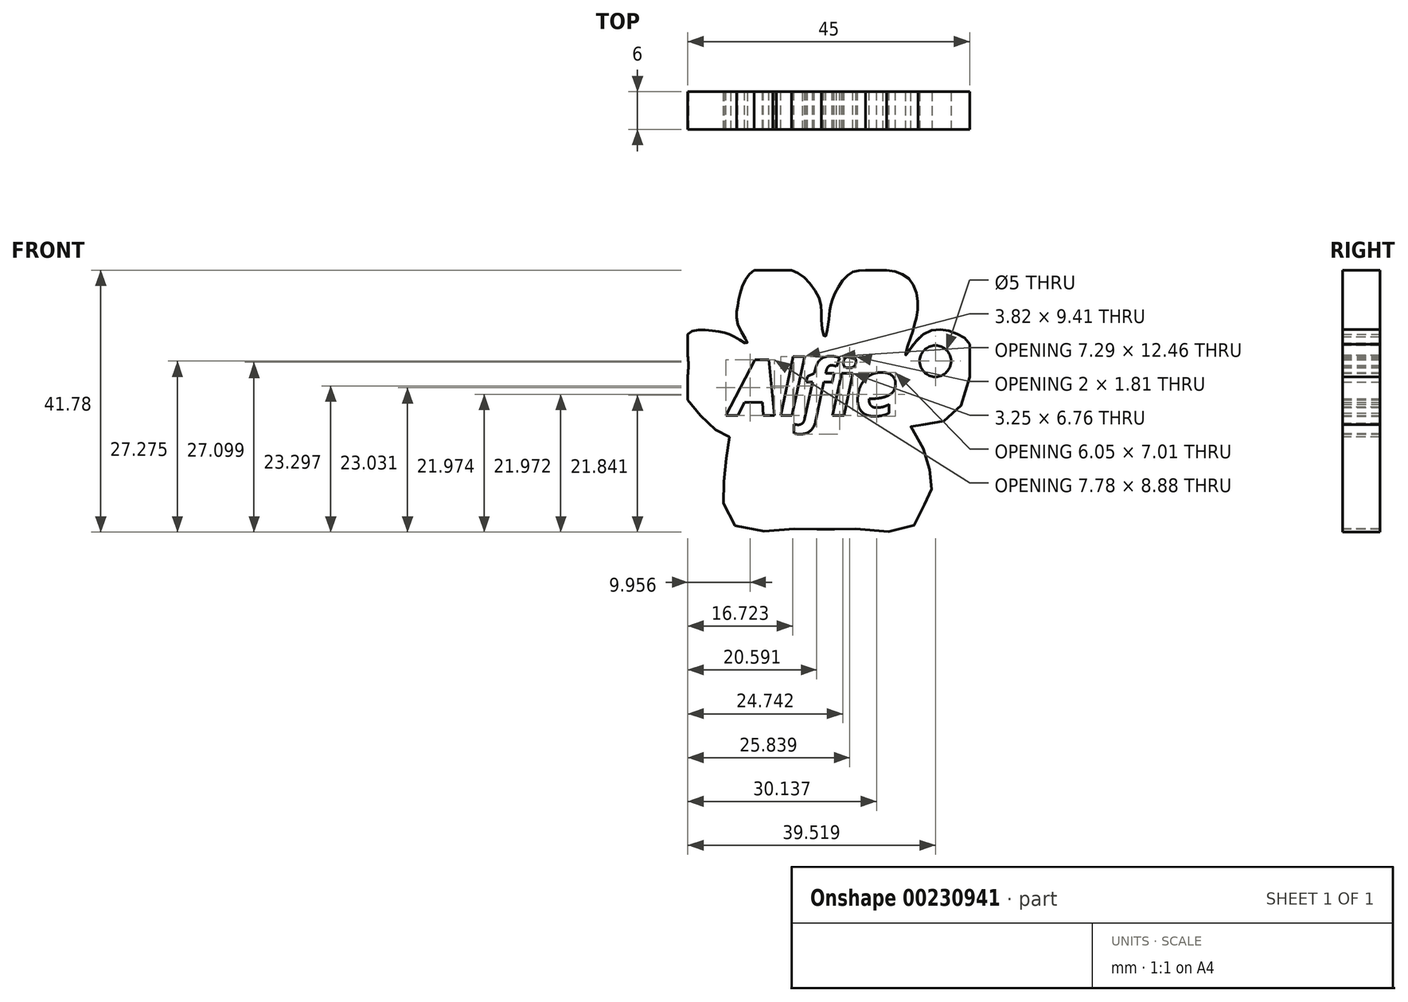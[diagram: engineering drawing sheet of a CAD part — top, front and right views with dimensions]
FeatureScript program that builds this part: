
annotation { "Feature Type Name" : "Feature", "Feature Type Description" : "" }
export const myFeature = defineFeature(function(context is Context, id is Id, definition is map)
    precondition{}
    {
        {
            var Q0;
            Q0=qCreatedBy(makeId("Front.planeOp"),FACE);
            var sketch = newSketch(context, id + "F0", { "sketchPlane" : qUnion([Q0])});
            skLineSegment(sketch, "E0.bottom", {"start": v(-5.8, 13.59) * mm, "end": v(39.2, 13.59) * mm});
            skLineSegment(sketch, "E0.top", {"start": v(-5.8, -31.41) * mm, "end": v(39.2, -31.41) * mm});
            skLineSegment(sketch, "E0.left", {"start": v(-5.8, 13.59) * mm, "end": v(-5.8, -31.41) * mm});
            skLineSegment(sketch, "E0.right", {"start": v(39.2, 13.59) * mm, "end": v(39.2, -31.41) * mm});
            skPoint(sketch, "E1.34.internal.snap0", {"position": v(39.2, -8.91) * mm});
            skFitSpline(sketch, "E1", {"points": [v(-4.05, -9.34) * mm, v(-5.8, -7.09) * mm, v(-5.8, -3.27) * mm, v(-5.8, 0) * mm, v(-5.8, 3.35) * mm, v(-3.2, 4.06) * mm, v(0, 3.63) * mm, v(2, 2.79) * mm, v(3.7, 1.94) * mm, v(2.29, 4.76) * mm, v(2.15, 7.72) * mm, v(2.85, 10.82) * mm, v(4.83, 13.59) * mm, v(7.79, 13.59) * mm, v(10.75, 13.59) * mm, v(13.43, 11.8) * mm, v(15.4, 8.43) * mm, v(15.54, 5.18) * mm, v(16.1, 2.93) * mm, v(16.8, 6.6) * mm, v(17.23, 8.7) * mm, v(18.36, 11.1) * mm, v(20.33, 13.22) * mm, v(22.59, 13.59) * mm, v(25.97, 13.59) * mm, v(29.36, 12.37) * mm, v(30.9, 8.85) * mm, v(30.48, 5.18) * mm, v(29.64, 2.36) * mm, v(28.93, 0) * mm, v(31.61, 3.21) * mm, v(35.84, 3.92) * mm, v(39.2, 1.8) * mm, v(39.2, -3.42) * mm, v(37.25, -8.91) * mm, v(34.3, -10.75) * mm, v(31.33, -11.03) * mm, v(29.78, -11.03) * mm, v(31.33, -13.99) * mm, v(32.6, -17.37) * mm, v(33.16, -20.47) * mm, v(32.88, -22.3) * mm, v(31.61, -24.56) * mm, v(29.64, -27.76) * mm, v(22.87, -27.76) * mm, v(18.22, -27.76) * mm, v(16.7, -27.76) * mm, v(13.85, -27.76) * mm, v(9.76, -27.76) * mm, v(2.85, -27.76) * mm, v(0, -24.28) * mm, v(0, -20.61) * mm, v(0, -17.8) * mm, v(1.02, -13.14) * mm, v(0, -13) * mm, v(-1.8, -11.3) * mm, v(-4.05, -9.34) * mm]});
            skText(sketch, "E2", { "text": "Alfie", "fontName": "OpenSans-BoldItalic.ttf"});
            const initialGuessF0  = {"E2": [0.00102, -0.0096, 1, 0, 0.00892]};
            skSetInitialGuess(sketch, initialGuessF0);
            skSolve(sketch);
        }
        {
            var Q0;
            Q0=makeQuery(id+"F0.imprint","IMPRINT",FACE,{"disambiguationData":[TD([[makeQuery(id+"F0.imprint","IMPRINT",EDGE,{"derivedFrom":sQuery(id+"F0.wireOp",EDGE,"E2.sketch_text.stroke-0")}),1.0]])]});
            var Q1;
            Q1=sQuery(id+"F0.wireOp",EDGE,"E1");
            extrude(context, id + "F1", {"entities" : qUnion([Q0]), "surfaceEntities" : qUnion([Q1]), "depth" : 6 * mm});
        }
        {
            var Q0;
            Q0=makeQuery(id+"F1.opExtrude","CAP_FACE",FACE,{"disambiguationData":[OSD([sQuery(id+"F0.wireOp",EDGE,"E0.bottom"),sQuery(id+"F0.wireOp",EDGE,"E0.left"),sQuery(id+"F0.wireOp",EDGE,"E0.right"),sQuery(id+"F0.wireOp",EDGE,"E1"),sQuery(id+"F0.wireOp",EDGE,"E2.sketch_text.stroke-0"),sQuery(id+"F0.wireOp",EDGE,"E2.sketch_text.stroke-1"),sQuery(id+"F0.wireOp",EDGE,"E2.sketch_text.stroke-2"),sQuery(id+"F0.wireOp",EDGE,"E2.sketch_text.stroke-3"),sQuery(id+"F0.wireOp",EDGE,"E2.sketch_text.stroke-4"),sQuery(id+"F0.wireOp",EDGE,"E2.sketch_text.stroke-5"),sQuery(id+"F0.wireOp",EDGE,"E2.sketch_text.stroke-6"),sQuery(id+"F0.wireOp",EDGE,"E2.sketch_text.stroke-7"),sQuery(id+"F0.wireOp",EDGE,"E2.sketch_text.stroke-14"),sQuery(id+"F0.wireOp",EDGE,"E2.sketch_text.stroke-15"),sQuery(id+"F0.wireOp",EDGE,"E2.sketch_text.stroke-16"),sQuery(id+"F0.wireOp",EDGE,"E2.sketch_text.stroke-17"),sQuery(id+"F0.wireOp",EDGE,"E2.sketch_text.stroke-18"),sQuery(id+"F0.wireOp",EDGE,"E2.sketch_text.stroke-19"),sQuery(id+"F0.wireOp",EDGE,"E2.sketch_text.stroke-20"),sQuery(id+"F0.wireOp",EDGE,"E2.sketch_text.stroke-21"),sQuery(id+"F0.wireOp",EDGE,"E2.sketch_text.stroke-22"),sQuery(id+"F0.wireOp",EDGE,"E2.sketch_text.stroke-23"),sQuery(id+"F0.wireOp",EDGE,"E2.sketch_text.stroke-24"),sQuery(id+"F0.wireOp",EDGE,"E2.sketch_text.stroke-25"),sQuery(id+"F0.wireOp",EDGE,"E2.sketch_text.stroke-26"),sQuery(id+"F0.wireOp",EDGE,"E2.sketch_text.stroke-27"),sQuery(id+"F0.wireOp",EDGE,"E2.sketch_text.stroke-28"),sQuery(id+"F0.wireOp",EDGE,"E2.sketch_text.stroke-29"),sQuery(id+"F0.wireOp",EDGE,"E2.sketch_text.stroke-30"),sQuery(id+"F0.wireOp",EDGE,"E2.sketch_text.stroke-31"),sQuery(id+"F0.wireOp",EDGE,"E2.sketch_text.stroke-32"),sQuery(id+"F0.wireOp",EDGE,"E2.sketch_text.stroke-33"),sQuery(id+"F0.wireOp",EDGE,"E2.sketch_text.stroke-34"),sQuery(id+"F0.wireOp",EDGE,"E2.sketch_text.stroke-35"),sQuery(id+"F0.wireOp",EDGE,"E2.sketch_text.stroke-36"),sQuery(id+"F0.wireOp",EDGE,"E2.sketch_text.stroke-37"),sQuery(id+"F0.wireOp",EDGE,"E2.sketch_text.stroke-38"),sQuery(id+"F0.wireOp",EDGE,"E2.sketch_text.stroke-39"),sQuery(id+"F0.wireOp",EDGE,"E2.sketch_text.stroke-40"),sQuery(id+"F0.wireOp",EDGE,"E2.sketch_text.stroke-41"),sQuery(id+"F0.wireOp",EDGE,"E2.sketch_text.stroke-42"),sQuery(id+"F0.wireOp",EDGE,"E2.sketch_text.stroke-43"),sQuery(id+"F0.wireOp",EDGE,"E2.sketch_text.stroke-44"),sQuery(id+"F0.wireOp",EDGE,"E2.sketch_text.stroke-45"),sQuery(id+"F0.wireOp",EDGE,"E2.sketch_text.stroke-46"),sQuery(id+"F0.wireOp",EDGE,"E2.sketch_text.stroke-47"),sQuery(id+"F0.wireOp",EDGE,"E2.sketch_text.stroke-48"),sQuery(id+"F0.wireOp",EDGE,"E2.sketch_text.stroke-49"),sQuery(id+"F0.wireOp",EDGE,"E2.sketch_text.stroke-50"),sQuery(id+"F0.wireOp",EDGE,"E2.sketch_text.stroke-51"),sQuery(id+"F0.wireOp",EDGE,"E2.sketch_text.stroke-58"),sQuery(id+"F0.wireOp",EDGE,"E2.sketch_text.stroke-59"),sQuery(id+"F0.wireOp",EDGE,"E2.sketch_text.stroke-60"),sQuery(id+"F0.wireOp",EDGE,"E2.sketch_text.stroke-61"),sQuery(id+"F0.wireOp",EDGE,"E2.sketch_text.stroke-62"),sQuery(id+"F0.wireOp",EDGE,"E2.sketch_text.stroke-63"),sQuery(id+"F0.wireOp",EDGE,"E2.sketch_text.stroke-64"),sQuery(id+"F0.wireOp",EDGE,"E2.sketch_text.stroke-65"),sQuery(id+"F0.wireOp",EDGE,"E2.sketch_text.stroke-66"),sQuery(id+"F0.wireOp",EDGE,"E2.sketch_text.stroke-67"),sQuery(id+"F0.wireOp",EDGE,"E2.sketch_text.stroke-68"),sQuery(id+"F0.wireOp",EDGE,"E2.sketch_text.stroke-69"),sQuery(id+"F0.wireOp",EDGE,"E2.sketch_text.stroke-70"),sQuery(id+"F0.wireOp",EDGE,"E2.sketch_text.stroke-71"),sQuery(id+"F0.wireOp",EDGE,"E2.sketch_text.stroke-72"),sQuery(id+"F0.wireOp",EDGE,"E2.sketch_text.stroke-73"),sQuery(id+"F0.wireOp",EDGE,"E2.sketch_text.stroke-74"),sQuery(id+"F0.wireOp",EDGE,"E2.sketch_text.stroke-75")])],"isStart":false});
            var sketch = newSketch(context, id + "F2", { "sketchPlane" : qUnion([Q0])});
            skPoint(sketch, "E3", {"position": v(33.73, -0.92) * mm});
            skSolve(sketch);
        }
        {
            var Q0;
            Q0=sQuery(id+"F2.wireOp",VERTEX,"E3");
            var Q1;
            Q1=makeQuery(id+"F1.opExtrude","SWEPT_BODY",BODY,{"disambiguationData":[OSD([sQuery(id+"F0.wireOp",EDGE,"E0.bottom"),sQuery(id+"F0.wireOp",EDGE,"E0.left"),sQuery(id+"F0.wireOp",EDGE,"E0.right"),sQuery(id+"F0.wireOp",EDGE,"E1"),sQuery(id+"F0.wireOp",EDGE,"E2.sketch_text.stroke-0"),sQuery(id+"F0.wireOp",EDGE,"E2.sketch_text.stroke-1"),sQuery(id+"F0.wireOp",EDGE,"E2.sketch_text.stroke-2"),sQuery(id+"F0.wireOp",EDGE,"E2.sketch_text.stroke-3"),sQuery(id+"F0.wireOp",EDGE,"E2.sketch_text.stroke-4"),sQuery(id+"F0.wireOp",EDGE,"E2.sketch_text.stroke-5"),sQuery(id+"F0.wireOp",EDGE,"E2.sketch_text.stroke-6"),sQuery(id+"F0.wireOp",EDGE,"E2.sketch_text.stroke-7"),sQuery(id+"F0.wireOp",EDGE,"E2.sketch_text.stroke-14"),sQuery(id+"F0.wireOp",EDGE,"E2.sketch_text.stroke-15"),sQuery(id+"F0.wireOp",EDGE,"E2.sketch_text.stroke-16"),sQuery(id+"F0.wireOp",EDGE,"E2.sketch_text.stroke-17"),sQuery(id+"F0.wireOp",EDGE,"E2.sketch_text.stroke-18"),sQuery(id+"F0.wireOp",EDGE,"E2.sketch_text.stroke-19"),sQuery(id+"F0.wireOp",EDGE,"E2.sketch_text.stroke-20"),sQuery(id+"F0.wireOp",EDGE,"E2.sketch_text.stroke-21"),sQuery(id+"F0.wireOp",EDGE,"E2.sketch_text.stroke-22"),sQuery(id+"F0.wireOp",EDGE,"E2.sketch_text.stroke-23"),sQuery(id+"F0.wireOp",EDGE,"E2.sketch_text.stroke-24"),sQuery(id+"F0.wireOp",EDGE,"E2.sketch_text.stroke-25"),sQuery(id+"F0.wireOp",EDGE,"E2.sketch_text.stroke-26"),sQuery(id+"F0.wireOp",EDGE,"E2.sketch_text.stroke-27"),sQuery(id+"F0.wireOp",EDGE,"E2.sketch_text.stroke-28"),sQuery(id+"F0.wireOp",EDGE,"E2.sketch_text.stroke-29"),sQuery(id+"F0.wireOp",EDGE,"E2.sketch_text.stroke-30"),sQuery(id+"F0.wireOp",EDGE,"E2.sketch_text.stroke-31"),sQuery(id+"F0.wireOp",EDGE,"E2.sketch_text.stroke-32"),sQuery(id+"F0.wireOp",EDGE,"E2.sketch_text.stroke-33"),sQuery(id+"F0.wireOp",EDGE,"E2.sketch_text.stroke-34"),sQuery(id+"F0.wireOp",EDGE,"E2.sketch_text.stroke-35"),sQuery(id+"F0.wireOp",EDGE,"E2.sketch_text.stroke-36"),sQuery(id+"F0.wireOp",EDGE,"E2.sketch_text.stroke-37"),sQuery(id+"F0.wireOp",EDGE,"E2.sketch_text.stroke-38"),sQuery(id+"F0.wireOp",EDGE,"E2.sketch_text.stroke-39"),sQuery(id+"F0.wireOp",EDGE,"E2.sketch_text.stroke-40"),sQuery(id+"F0.wireOp",EDGE,"E2.sketch_text.stroke-41"),sQuery(id+"F0.wireOp",EDGE,"E2.sketch_text.stroke-42"),sQuery(id+"F0.wireOp",EDGE,"E2.sketch_text.stroke-43"),sQuery(id+"F0.wireOp",EDGE,"E2.sketch_text.stroke-44"),sQuery(id+"F0.wireOp",EDGE,"E2.sketch_text.stroke-45"),sQuery(id+"F0.wireOp",EDGE,"E2.sketch_text.stroke-46"),sQuery(id+"F0.wireOp",EDGE,"E2.sketch_text.stroke-47"),sQuery(id+"F0.wireOp",EDGE,"E2.sketch_text.stroke-48"),sQuery(id+"F0.wireOp",EDGE,"E2.sketch_text.stroke-49"),sQuery(id+"F0.wireOp",EDGE,"E2.sketch_text.stroke-50"),sQuery(id+"F0.wireOp",EDGE,"E2.sketch_text.stroke-51"),sQuery(id+"F0.wireOp",EDGE,"E2.sketch_text.stroke-58"),sQuery(id+"F0.wireOp",EDGE,"E2.sketch_text.stroke-59"),sQuery(id+"F0.wireOp",EDGE,"E2.sketch_text.stroke-60"),sQuery(id+"F0.wireOp",EDGE,"E2.sketch_text.stroke-61"),sQuery(id+"F0.wireOp",EDGE,"E2.sketch_text.stroke-62"),sQuery(id+"F0.wireOp",EDGE,"E2.sketch_text.stroke-63"),sQuery(id+"F0.wireOp",EDGE,"E2.sketch_text.stroke-64"),sQuery(id+"F0.wireOp",EDGE,"E2.sketch_text.stroke-65"),sQuery(id+"F0.wireOp",EDGE,"E2.sketch_text.stroke-66"),sQuery(id+"F0.wireOp",EDGE,"E2.sketch_text.stroke-67"),sQuery(id+"F0.wireOp",EDGE,"E2.sketch_text.stroke-68"),sQuery(id+"F0.wireOp",EDGE,"E2.sketch_text.stroke-69"),sQuery(id+"F0.wireOp",EDGE,"E2.sketch_text.stroke-70"),sQuery(id+"F0.wireOp",EDGE,"E2.sketch_text.stroke-71"),sQuery(id+"F0.wireOp",EDGE,"E2.sketch_text.stroke-72"),sQuery(id+"F0.wireOp",EDGE,"E2.sketch_text.stroke-73"),sQuery(id+"F0.wireOp",EDGE,"E2.sketch_text.stroke-74"),sQuery(id+"F0.wireOp",EDGE,"E2.sketch_text.stroke-75")])]});
            hole(context, id + "F3", {"style" : HoleStyle.SIMPLE, "endStyle" : HoleEndStyle.THROUGH, "holeDiameter" : 5 * mm, "locations" : qUnion([Q0]), "scope" : qUnion([Q1]), "isTappedThrough" : true});
        }
    });
